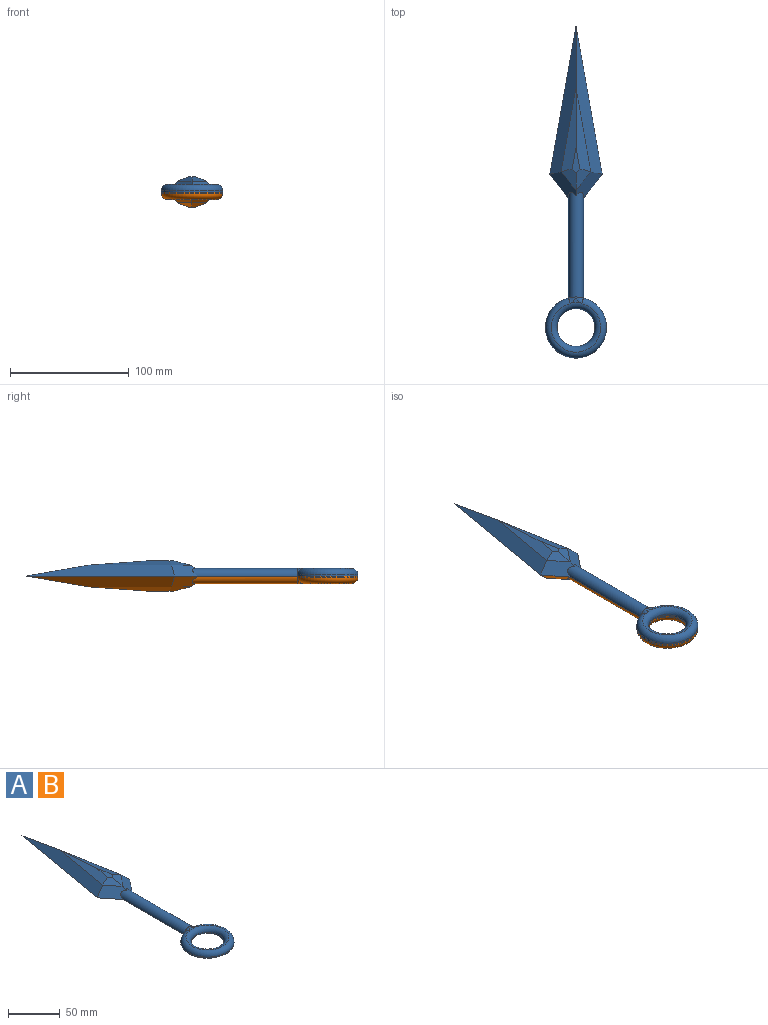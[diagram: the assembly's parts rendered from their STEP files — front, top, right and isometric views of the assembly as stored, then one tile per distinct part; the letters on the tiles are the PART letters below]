
ASSEMBLY  parts=2 mates=1
PART A: 18 faces, bbox 55.7x281.8x15 mm
  f0: cylinder r=6.35mm len=89.04mm, axis (0,1,0), area 1741.3mm2, adj f2,f5,f6,f7,f10,f12
  f1: plane 21.96x6.33mm, normal (0,0,1), area 69.4mm2, adj f14,f15,f16,f17
  f2: plane 279.72x51.44mm, normal (0,0,-1), area 5672mm2, adj f0,f3,f4,f5,f6,f7,f8
  f3: plane 125.07x22.05mm, normal (0.7,0.12,0.71), area 1276.9mm2, adj f2,f4,f5,f17
  f4: plane 125.07x22.05mm, normal (-0.7,0.12,0.71), area 1276.9mm2, adj f2,f3,f6,f16
  f5: plane 22.39x22.05mm, normal (0.56,-0.44,0.71), area 286.2mm2, adj f0,f2,f3,f6,f15
  f6: plane 22.39x22.05mm, normal (-0.56,-0.44,0.71), area 286.2mm2, adj f0,f2,f4,f5,f14
  f7: cylinder r=25.72mm len=51.44mm, axis (0,0,-1), area 189.1mm2, adj f0,f2,f11
  f8: cylinder r=15.88mm len=31.75mm, axis (0,0,-1), area 126.7mm2, adj f2,f13
  f9: plane 6.94x5.06mm, normal (0,0,1), area 12.2mm2, adj f10,f12,f13
  f10: bspline ~6.26x5.84mm, area 24.8mm2, adj f0,f9,f11,f13
  f11: torus R=20.64mm, axis (0,0,1), area 1084.7mm2, adj f7,f10,f12,f13
  f12: bspline ~6.26x5.81mm, area 24.7mm2, adj f0,f9,f11,f13
  f13: torus R=20.96mm, axis (0,0,1), area 869mm2, adj f8,f9,f10,f11,f12
  f14: plane 18.05x12.38mm, normal (-0.3,-0.24,0.92), area 118mm2, adj f1,f6,f15,f16
  f15: plane 18.05x12.38mm, normal (0.3,-0.24,0.92), area 118mm2, adj f1,f5,f14,f17
  f16: plane 70.19x12.38mm, normal (-0.38,0.07,0.92), area 420mm2, adj f1,f4,f14,f17
  f17: plane 70.19x12.38mm, normal (0.38,0.07,0.92), area 420mm2, adj f1,f3,f15,f16
PART B: same geometry as A
PLACE A t=(7.88,20.43,-5.64)mm
PLACE B rot(axis=(0,1,0),180deg) t=(7.88,20.43,-5.64)mm
MATE fastened B.f2 <-> A.f2  axis (0,0,1) through (7.88,-1.51,-5.64)mm
